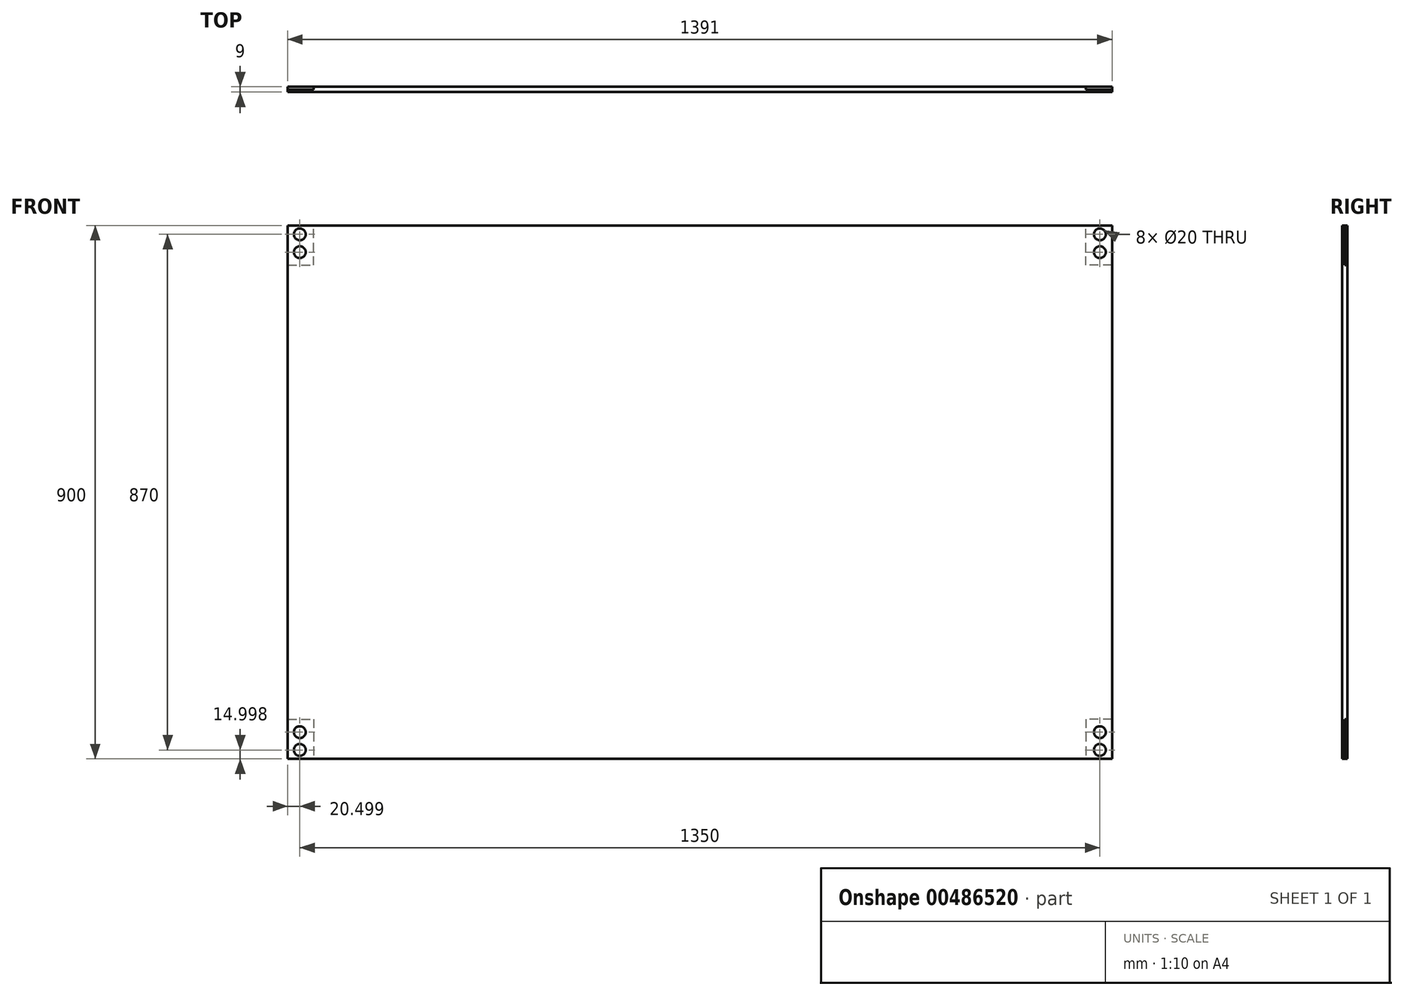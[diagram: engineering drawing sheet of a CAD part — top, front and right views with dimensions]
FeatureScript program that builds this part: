
annotation { "Feature Type Name" : "Feature", "Feature Type Description" : "" }
export const myFeature = defineFeature(function(context is Context, id is Id, definition is map)
    precondition{}
    {
        {
            var Q0;
            Q0=qCreatedBy(makeId("Front.planeOp"),FACE);
            var sketch = newSketch(context, id + "F0", { "sketchPlane" : qUnion([Q0])});
            skLineSegment(sketch, "E0.bottom", {"start": v(-688.57, 488.98) * mm, "end": v(702.43, 488.98) * mm});
            skLineSegment(sketch, "E0.top", {"start": v(-688.57, -411.02) * mm, "end": v(702.43, -411.02) * mm});
            skLineSegment(sketch, "E0.left", {"start": v(-688.57, 488.98) * mm, "end": v(-688.57, -411.02) * mm});
            skLineSegment(sketch, "E0.right", {"start": v(702.43, 488.98) * mm, "end": v(702.43, -411.02) * mm});
            skLineSegment(sketch, "E1", {"start": v(-688.57, 421.98) * mm, "end": v(-644.57, 421.98) * mm});
            skLineSegment(sketch, "E2", {"start": v(-644.57, 421.98) * mm, "end": v(-644.57, 488.98) * mm});
            skLineSegment(sketch, "E3", {"start": v(702.43, 421.98) * mm, "end": v(658.43, 421.98) * mm});
            skLineSegment(sketch, "E4", {"start": v(658.43, 421.98) * mm, "end": v(658.43, 488.98) * mm});
            skCircle(sketch, "E5", {"center": v(-668.07, 473.98) * mm, "radius": 10 * mm});
            skCircle(sketch, "E6", {"center": v(-668.07, 443.98) * mm, "radius": 10 * mm});
            skCircle(sketch, "E7", {"center": v(681.93, 473.98) * mm, "radius": 10 * mm});
            skCircle(sketch, "E8", {"center": v(681.93, 443.98) * mm, "radius": 10 * mm});
            skLineSegment(sketch, "E9.MirrorCS", {"start": v(-688.57, -344.02) * mm, "end": v(-644.57, -344.02) * mm});
            skLineSegment(sketch, "E10.MirrorCS", {"start": v(-644.57, -344.02) * mm, "end": v(-644.57, -411.02) * mm});
            skCircle(sketch, "E11.MirrorC", {"center": v(-668.07, -366.02) * mm, "radius": 10 * mm});
            skCircle(sketch, "E12.MirrorC", {"center": v(-668.07, -396.02) * mm, "radius": 10 * mm});
            skLineSegment(sketch, "E13.MirrorCS", {"start": v(702.43, -344.02) * mm, "end": v(658.43, -344.02) * mm});
            skLineSegment(sketch, "E14.MirrorCS", {"start": v(658.43, -344.02) * mm, "end": v(658.43, -411.02) * mm});
            skCircle(sketch, "E15.MirrorC", {"center": v(681.93, -366.02) * mm, "radius": 10 * mm});
            skCircle(sketch, "E16.MirrorC", {"center": v(681.93, -396.02) * mm, "radius": 10 * mm});
            skSolve(sketch);
        }
        {
            var Q0;
            {var subQ1=sQuery(id+"F0.wireOp",EDGE,"aKvIycwU-4pN5-MguQ-l09Z-TlI6qNkUzQiX");Q0=makeQuery(id+"F0.imprint","IMPRINT",FACE,{"disambiguationData":[TD([[makeQuery(id+"F0.imprint","IMPRINT",EDGE,{"derivedFrom":subQ1}),1.0]])]});}
            var Q1;
            {var subQ2=sQuery(id+"F0.wireOp",EDGE,"E1");Q1=makeQuery(id+"F0.imprint","IMPRINT",FACE,{"disambiguationData":[TD([[makeQuery(id+"F0.imprint","IMPRINT",EDGE,{"derivedFrom":subQ2}),-1.0]])]});}
            var Q2;
            {var subQ0=sQuery(id+"F0.wireOp",EDGE,"TBAXlU3e-xU2m-CWmv-7BMn-PrzSTU1MQoj6");Q2=makeQuery(id+"F0.imprint","IMPRINT",FACE,{"disambiguationData":[TD([[makeQuery(id+"F0.imprint","IMPRINT",EDGE,{"derivedFrom":subQ0}),-1.0]])]});}
            var Q3;
            Q3=makeQuery(id+"F0.imprint","IMPRINT",FACE,{"disambiguationData":[TD([[makeQuery(id+"F0.imprint","IMPRINT",EDGE,{"derivedFrom":sQuery(id+"F0.wireOp",EDGE,"E13.MirrorCS")}),1.0]])]});
            var Q4;
            {var subQ1=sQuery(id+"F0.wireOp",EDGE,"a006090f-7919-4436-a980-1e86cbb036050.MirrorCS");Q4=makeQuery(id+"F0.imprint","IMPRINT",FACE,{"disambiguationData":[TD([[makeQuery(id+"F0.imprint","IMPRINT",EDGE,{"derivedFrom":subQ1}),-1.0]])]});}
            var Q5;
            Q5=makeQuery(id+"F0.imprint","IMPRINT",FACE,{"disambiguationData":[TD([[makeQuery(id+"F0.imprint","IMPRINT",EDGE,{"derivedFrom":sQuery(id+"F0.wireOp",EDGE,"E1")}),1.0]])]});
            var Q6;
            {var subQ4=sQuery(id+"F0.wireOp",EDGE,"E3");Q6=makeQuery(id+"F0.imprint","IMPRINT",FACE,{"disambiguationData":[TD([[makeQuery(id+"F0.imprint","IMPRINT",EDGE,{"derivedFrom":subQ4}),-1.0]])]});}
            var Q7;
            {var subQ1=sQuery(id+"F0.wireOp",EDGE,"E9.MirrorCS");Q7=makeQuery(id+"F0.imprint","IMPRINT",FACE,{"disambiguationData":[TD([[makeQuery(id+"F0.imprint","IMPRINT",EDGE,{"derivedFrom":subQ1}),-1.0]])]});}
            extrude(context, id + "F1", {"entities" : qUnion([Q0, Q1, Q2, Q3, Q4, Q5, Q6, Q7]), "depth" : 9 * mm, "offsetDistance" : 25 * mm});
        }
        {
            var Q0;
            {var subQ0=sQuery(id+"F0.wireOp",EDGE,"aKvIycwU-4pN5-MguQ-l09Z-TlI6qNkUzQiX");Q0=makeQuery(id+"F0.imprint","IMPRINT",FACE,{"disambiguationData":[TD([[makeQuery(id+"F0.imprint","IMPRINT",EDGE,{"derivedFrom":subQ0}),1.0]])]});}
            var Q1;
            {var subQ0=sQuery(id+"F0.wireOp",EDGE,"TBAXlU3e-xU2m-CWmv-7BMn-PrzSTU1MQoj6");Q1=makeQuery(id+"F0.imprint","IMPRINT",FACE,{"disambiguationData":[TD([[makeQuery(id+"F0.imprint","IMPRINT",EDGE,{"derivedFrom":subQ0}),-1.0]])]});}
            var Q2;
            {var subQ1=sQuery(id+"F0.wireOp",EDGE,"a006090f-7919-4436-a980-1e86cbb036050.MirrorCS");Q2=makeQuery(id+"F0.imprint","IMPRINT",FACE,{"disambiguationData":[TD([[makeQuery(id+"F0.imprint","IMPRINT",EDGE,{"derivedFrom":subQ1}),-1.0]])]});}
            var Q3;
            Q3=makeQuery(id+"F0.imprint","IMPRINT",FACE,{"disambiguationData":[TD([[makeQuery(id+"F0.imprint","IMPRINT",EDGE,{"derivedFrom":sQuery(id+"F0.wireOp",EDGE,"E13.MirrorCS")}),1.0]])]});
            var Q4;
            Q4=makeQuery(id+"F0.imprint","IMPRINT",FACE,{"disambiguationData":[TD([[makeQuery(id+"F0.imprint","IMPRINT",EDGE,{"derivedFrom":sQuery(id+"F0.wireOp",EDGE,"E1")}),1.0]])]});
            var Q5;
            {var subQ4=sQuery(id+"F0.wireOp",EDGE,"E3");Q5=makeQuery(id+"F0.imprint","IMPRINT",FACE,{"disambiguationData":[TD([[makeQuery(id+"F0.imprint","IMPRINT",EDGE,{"derivedFrom":subQ4}),-1.0]])]});}
            var Q6;
            {var subQ1=sQuery(id+"F0.wireOp",EDGE,"E9.MirrorCS");Q6=makeQuery(id+"F0.imprint","IMPRINT",FACE,{"disambiguationData":[TD([[makeQuery(id+"F0.imprint","IMPRINT",EDGE,{"derivedFrom":subQ1}),-1.0]])]});}
            extrude(context, id + "F2", {"entities" : qUnion([Q0, Q1, Q2, Q3, Q4, Q5, Q6]), "operationType" : NewBodyOperationType.REMOVE, "depth" : 5 * mm, "offsetDistance" : 25 * mm});
        }
    });
